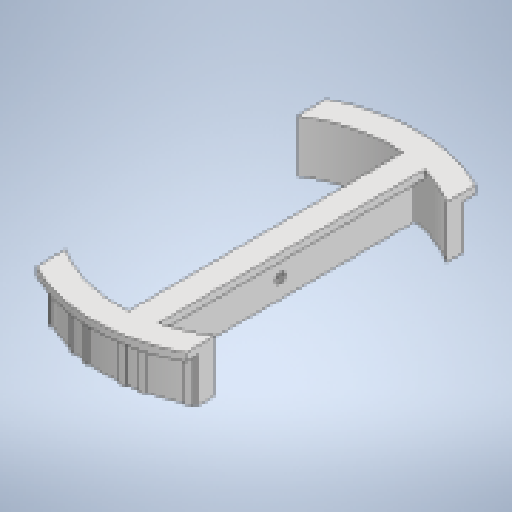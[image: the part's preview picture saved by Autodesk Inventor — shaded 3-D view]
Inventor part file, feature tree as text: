
AUTODESK INVENTOR PART (.ipt)
format: ipt  version: 2025 (Build 290162010, 162A)  size: 752,128 bytes
history: native  units: mm
features: sketch x11, extrude x10, pattern_circular x1, hole x1
ambient origin geometry x8: Origin, YZ Plane, XZ Plane, XY Plane, X Axis, Y Axis, Z Axis, Center Point
bodies: Solid1 (feature_tree)
feature tree (23):
  extrude  "Extrusion1"  Depth=15.0mm
  extrude  "Extrusion2"  Depth=25.0mm
  extrude  "Extrusion3"  TaperAngle=0.0deg  [1 undecoded]
  extrude  "Extrusion5"  Depth=78.1mm
  pattern_circular  "Circular Pattern1"  Count=18 Angle=360.0deg
  extrude  "Extrusion6"  Depth=83.0mm
  extrude  "Extrusion7"  Depth=13.75mm TaperAngle=0.0deg
  extrude  "Extrusion9"  Depth=70.0mm
  extrude  "Extrusion13"  Depth=10.0mm TaperAngle=0.0deg
  extrude  "Extrusion14"  Depth=6.604mm
  hole  "Hole3"  [1 undecoded]
  extrude  "Extrusion15"  Depth=2.0mm
  sketch  "Sketch1"  dims[d0=77.3mm d1=15.0mm]
  sketch  "Sketch2"  dims[d2=25.0mm d3=0.0mm d4=5.0mm]
  sketch  "Sketch3"  dims[d5=55.0mm d6=0.0mm d7=0.0mm]
  sketch  "Sketch9"  dims[d8=165.1mm d9=0.0mm d31=78.1mm]
  sketch  "Sketch11"  dims[d32=1.0mm d33=0.0mm d37=180.0mm d38=360.0deg]
  sketch  "Sketch12"  dims[d40=0.0mm d41=0.0mm d42=83.0mm]
  sketch  "Sketch14"  dims[d43=2.0mm d44=0.0mm d47=13.75mm d48=0.0mm]
  sketch  "Sketch18"  dims[d52=60.0mm d62=70.0mm]
  sketch  "Sketch19"  dims[d63=0.0mm d64=0.0mm d65=10.0mm d66=0.0mm]
  sketch  "Sketch20"  dims[d67=35.121mm d68=6.604mm]
  sketch  "Sketch21"  dims[d69=2.6416mm d70=7.01mm d71=4.0mm d72=2.0mm d73=90.0deg d74=10.979mm d75=0.0mm d76=0.0mm d77=0.0mm d56=0.5mm d57=0.872665mm d58=0.5mm d59=0.872665mm d60=0.872665mm d61=0.5mm]
note: 2 required parameter values undecoded (feature->parameter linkage not recoverable at this tier; creation-order binding heuristic only, values carry confidence <= 0.55)
